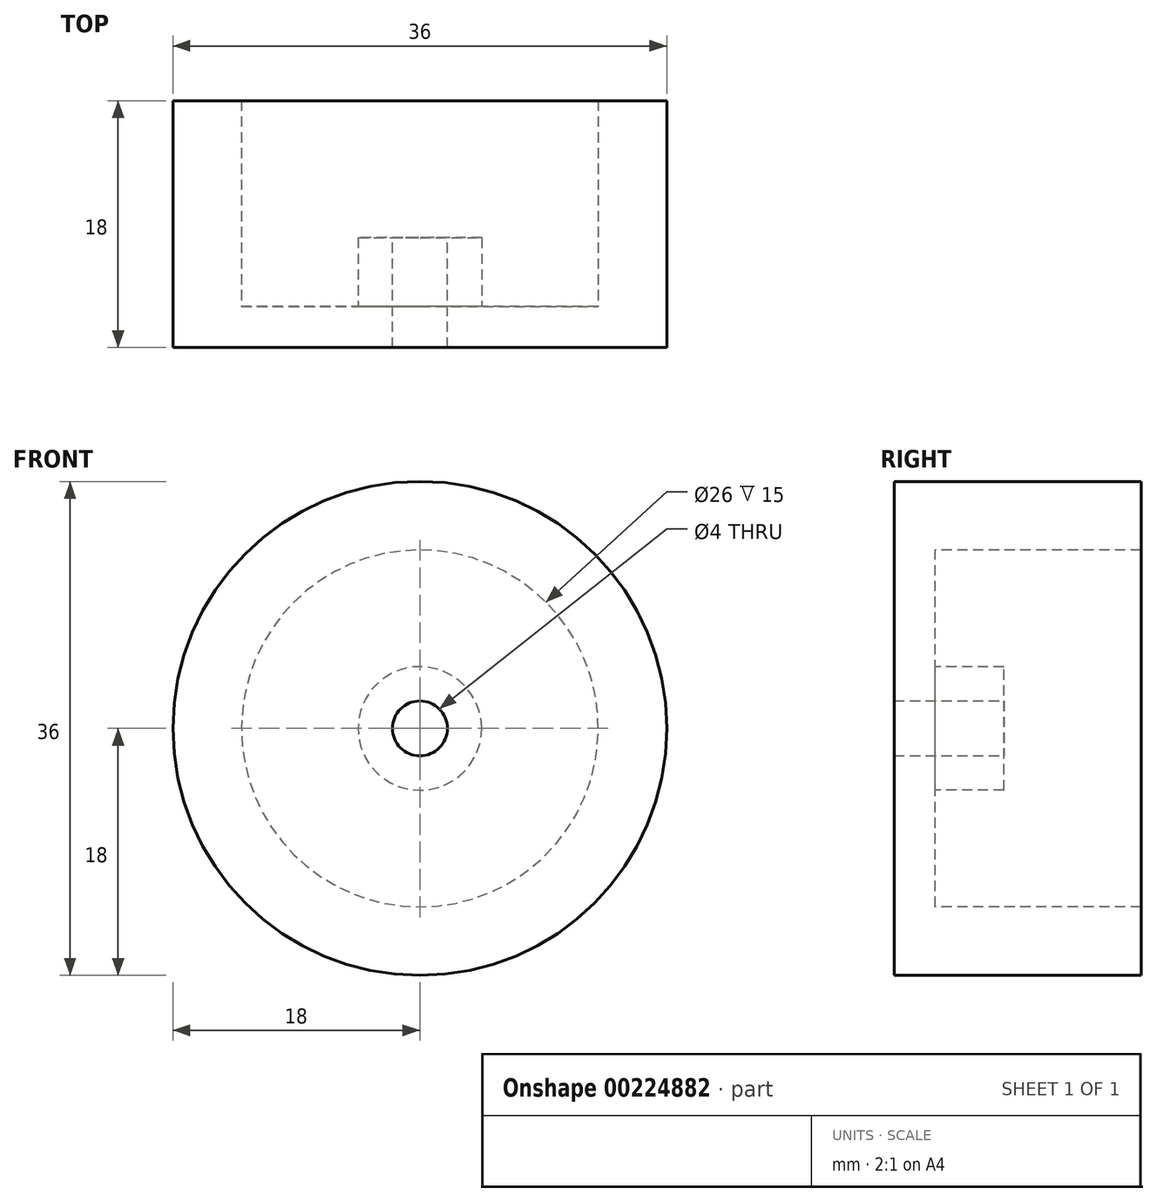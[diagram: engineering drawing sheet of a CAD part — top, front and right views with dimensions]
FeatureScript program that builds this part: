
annotation { "Feature Type Name" : "Feature", "Feature Type Description" : "" }
export const myFeature = defineFeature(function(context is Context, id is Id, definition is map)
    precondition{}
    {
        {
            var Q0;
            Q0=qCreatedBy(makeId("Right.planeOp"),FACE);
            var sketch = newSketch(context, id + "F0", { "sketchPlane" : qUnion([Q0])});
            skLineSegment(sketch, "E0", {"start": v(0, 0) * mm, "end": v(0, 18) * mm});
            skLineSegment(sketch, "E1", {"start": v(0, 18) * mm, "end": v(18, 18) * mm});
            skLineSegment(sketch, "E2", {"start": v(18, 18) * mm, "end": v(18, 13) * mm});
            skLineSegment(sketch, "E3", {"start": v(18, 13) * mm, "end": v(3, 13) * mm});
            skLineSegment(sketch, "E4", {"start": v(3, 13) * mm, "end": v(3, 4.5) * mm});
            skLineSegment(sketch, "E5", {"start": v(3, 4.5) * mm, "end": v(8, 4.5) * mm});
            skLineSegment(sketch, "E6", {"start": v(8, 4.5) * mm, "end": v(8, 0) * mm});
            skLineSegment(sketch, "E7", {"start": v(8, 0) * mm, "end": v(0, 0) * mm});
            skSolve(sketch);
        }
        {
            var Q0;
            Q0=qCreatedBy(makeId("Right.planeOp"),FACE);
            var sketch = newSketch(context, id + "F1", { "sketchPlane" : qUnion([Q0])});
            skLineSegment(sketch, "E8", {"start": v(-75.44, 0) * mm, "end": v(73.54, 0) * mm, "construction": true});
            skSolve(sketch);
        }
        {
            var Q0;
            Q0=makeQuery(id+"F0.imprint","IMPRINT",FACE,{"disambiguationData":[TD([[makeQuery(id+"F0.imprint","IMPRINT",EDGE,{"derivedFrom":sQuery(id+"F0.wireOp",EDGE,"E0")}),-1.0]])]});
            var Q1;
            Q1=sQuery(id+"F1.wireOp",EDGE,"E8");
            revolve(context, id + "F2", {"entities" : qUnion([Q0]), "axis" : qUnion([Q1]), "revolveType" : RevolveType.FULL});
        }
        {
            var Q0;
            Q0=makeQuery(id+"F2.opRevolve","SWEPT_FACE",FACE,{"disambiguationData":[OSD([sQuery(id+"F0.wireOp",EDGE,"E6")])]});
            var sketch = newSketch(context, id + "F3", { "sketchPlane" : qUnion([Q0])});
            skCircle(sketch, "E9", {"center": v(0, 0) * mm, "radius": 2 * mm});
            skSolve(sketch);
        }
        {
            var Q0;
            Q0 = qSketchRegion(id + "F3", true);
            extrude(context, id + "F4", {"entities" : qUnion([Q0]), "operationType" : NewBodyOperationType.REMOVE, "oppositeDirection" : true, "depth" : 25 * mm});
        }
    });
